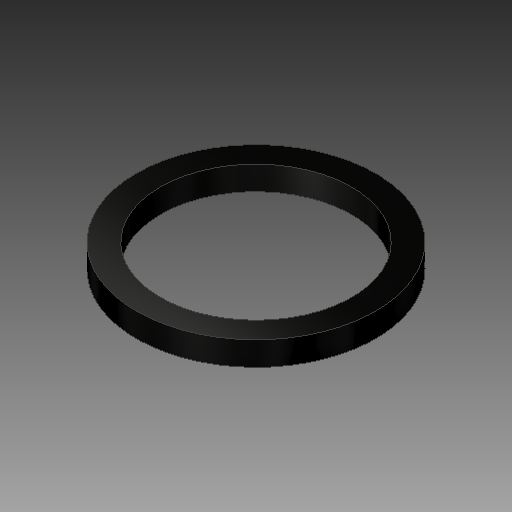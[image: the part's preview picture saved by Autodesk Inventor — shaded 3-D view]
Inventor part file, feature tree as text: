
AUTODESK INVENTOR PART (.ipt)
format: ipt  version: 2019.3 (Build 233278000, 278)  size: 104,960 bytes
history: native  units: mm
features: extrude x1, sketch x1
ambient origin geometry x8: Origin, YZ Plane, XZ Plane, XY Plane, X Axis, Y Axis, Z Axis, Center Point
bodies: Solid1 (feature_tree)
feature tree (2):
  extrude  "Extrusion1"  Depth=10.0mm
  sketch  "Sketch1"  dims[d0=8.0mm d1=10.0mm d2=1.0mm d3=0.0mm]
